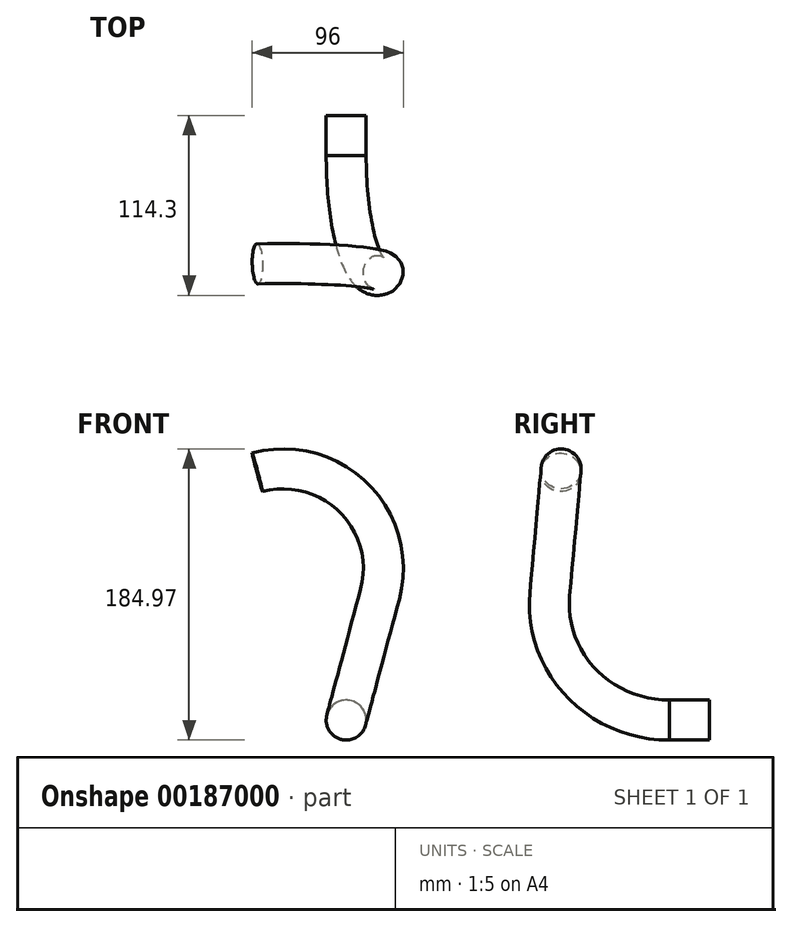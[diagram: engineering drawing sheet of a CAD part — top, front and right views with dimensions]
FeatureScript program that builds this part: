
annotation { "Feature Type Name" : "Feature", "Feature Type Description" : "" }
export const myFeature = defineFeature(function(context is Context, id is Id, definition is map)
    precondition{}
    {
        {
            var Q0;
            Q0=qCreatedBy(makeId("Front.planeOp"),FACE);
            var sketch = newSketch(context, id + "F0", { "sketchPlane" : qUnion([Q0])});
            skCircle(sketch, "E0", {"center": v(0, 0) * mm, "radius": 12.7 * mm});
            skSolve(sketch);
        }
        {
            var Q0;
            Q0=makeQuery(id+"F0.imprint","IMPRINT",FACE,{"disambiguationData":[TD([[makeQuery(id+"F0.imprint","IMPRINT",EDGE,{"derivedFrom":sQuery(id+"F0.wireOp",EDGE,"E0")}),1.0]])]});
            extrude(context, id + "F1", {"entities" : qUnion([Q0]), "depth" : 25.4 * mm});
        }
        {
            var Q0;
            Q0=makeQuery(id+"F1.opExtrude","CAP_FACE",FACE,{"disambiguationData":[OSD([sQuery(id+"F0.wireOp",EDGE,"E0")])],"isStart":false});
            var sketch = newSketch(context, id + "F2", { "sketchPlane" : qUnion([Q0])});
            skCircle(sketch, "E1.0", {"center": v(0, 0) * mm, "radius": 12.7 * mm});
            skLineSegment(sketch, "E2", {"start": v(0, 0) * mm, "end": v(19.72, 73.6) * mm, "construction": true});
            skLineSegment(sketch, "E3", {"start": v(19.72, 73.6) * mm, "end": v(41.47, 67.78) * mm, "construction": true});
            skSolve(sketch);
        }
        {
            var Q0;
            Q0=makeQuery(id+"F2.imprint","IMPRINT",FACE,{"disambiguationData":[TD([[makeQuery(id+"F2.imprint","IMPRINT",EDGE,{"derivedFrom":sQuery(id+"F2.wireOp",EDGE,"E1.0")}),1.0]])]});
            var Q1;
            Q1=sQuery(id+"F2.wireOp",EDGE,"E1.0");
            var Q2;
            Q2=sQuery(id+"F2.wireOp",EDGE,"E3");
            revolve(context, id + "F3", {"entities" : qUnion([Q0]), "surfaceEntities" : qUnion([Q1]), "axis" : qUnion([Q2]), "revolveType" : RevolveType.ONE_DIRECTION, "oppositeDirection" : true, "angle" : 95 * degree});
        }
        {
            var Q0;
            Q0=makeQuery(id+"F3.opRevolve","CAP_FACE",FACE,{"disambiguationData":[OSD([sQuery(id+"F2.wireOp",EDGE,"E1.0")])],"isStart":false});
            var sketch = newSketch(context, id + "F4", { "sketchPlane" : qUnion([Q0])});
            skLineSegment(sketch, "E4", {"start": v(2.52, -108.12) * mm, "end": v(-60.98, -108.12) * mm, "construction": true});
            skLineSegment(sketch, "E5", {"start": v(-60.98, -108.12) * mm, "end": v(-60.98, -81.87) * mm, "construction": true});
            skSolve(sketch);
        }
        {
            var Q0;
            Q0=makeQuery(id+"F4.imprint","IMPRINT",FACE,{"disambiguationData":[TD([[makeQuery(id+"F4.imprint","IMPRINT",EDGE,{"derivedFrom":makeQuery(id+"F3.opRevolve","CAP_EDGE",EDGE,{"disambiguationData":[OSD([sQuery(id+"F2.wireOp",EDGE,"E1.0")])],"isStart":false})}),1.0]])]});
            var Q1;
            Q1=sQuery(id+"F4.wireOp",EDGE,"E5");
            revolve(context, id + "F5", {"operationType" : NewBodyOperationType.ADD, "entities" : qUnion([Q0]), "axis" : qUnion([Q1]), "revolveType" : RevolveType.ONE_DIRECTION, "oppositeDirection" : true, "angle" : 120 * degree});
        }
    });
